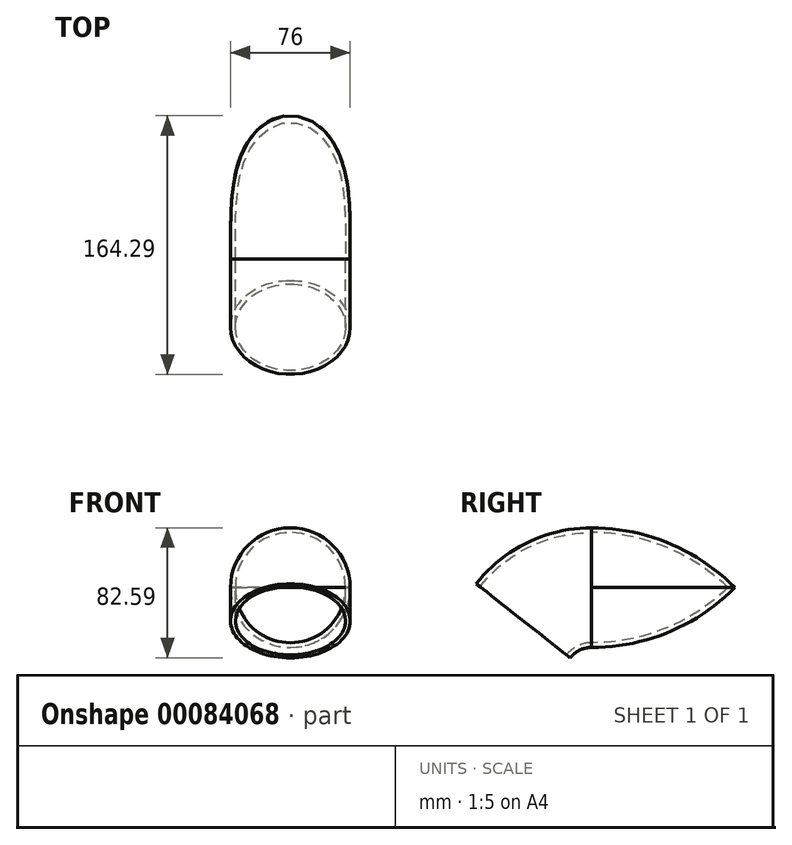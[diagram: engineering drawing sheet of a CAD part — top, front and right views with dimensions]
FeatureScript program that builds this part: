
annotation { "Feature Type Name" : "Feature", "Feature Type Description" : "" }
export const myFeature = defineFeature(function(context is Context, id is Id, definition is map)
    precondition{}
    {
        {
            var Q0;
            Q0=qCreatedBy(makeId("Front.planeOp"),FACE);
            var sketch = newSketch(context, id + "F0", { "sketchPlane" : qUnion([Q0])});
            skCircle(sketch, "E0", {"center": v(0, 0) * mm, "radius": 38 * mm});
            skCircle(sketch, "E1", {"center": v(0, 0) * mm, "radius": 35 * mm});
            skSolve(sketch);
        }
        {
            var Q0;
            Q0=qCreatedBy(makeId("Top.planeOp"),FACE);
            var sketch = newSketch(context, id + "F1", { "sketchPlane" : qUnion([Q0])});
            skLineSegment(sketch, "E2", {"start": v(90, 0) * mm, "end": v(90, 109) * mm, "construction": true});
            skArc(sketch, "E3", {"start": v(0, 0) * mm, "mid": v(26.36, 63.64) * mm, "end": v(90, 90) * mm});
            skSolve(sketch);
        }
        {
            var Q0;
            Q0=makeQuery(id+"F0.imprint","IMPRINT",FACE,{"disambiguationData":[TD([[makeQuery(id+"F0.imprint","IMPRINT",EDGE,{"derivedFrom":sQuery(id+"F0.wireOp",EDGE,"E0")}),1.0]])]});
            var Q1;
            Q1=sQuery(id+"F1.wireOp",EDGE,"E3");
            sweep(context, id + "F2", {"profiles" : qUnion([Q0]), "path" : qUnion([Q1])});
        }
        {
            var Q0;
            Q0=qCreatedBy(makeId("Top.planeOp"),FACE);
            var sketch = newSketch(context, id + "F3", { "sketchPlane" : qUnion([Q0])});
            skLineSegment(sketch, "E4", {"start": v(0, 0) * mm, "end": v(0, 200) * mm});
            skLineSegment(sketch, "E5", {"start": v(0, 200) * mm, "end": v(111.4, 200) * mm});
            skLineSegment(sketch, "E6", {"start": v(111.4, 200) * mm, "end": v(111.4, 0) * mm});
            skLineSegment(sketch, "E7", {"start": v(111.4, 0) * mm, "end": v(0, 0) * mm});
            skSolve(sketch);
        }
        {
            var Q0;
            Q0=makeQuery(id+"F3.imprint","IMPRINT",FACE,{"disambiguationData":[TD([[makeQuery(id+"F3.imprint","IMPRINT",EDGE,{"derivedFrom":sQuery(id+"F3.wireOp",EDGE,"E4")}),-1.0]])]});
            extrude(context, id + "F4", {"entities" : qUnion([Q0]), "operationType" : NewBodyOperationType.REMOVE, "endBound" : BoundingType.SYMMETRIC, "oppositeDirection" : true, "depth" : 200 * mm});
        }
        {
            var Q0;
            Q0=qCreatedBy(makeId("Right.planeOp"),FACE);
            var sketch = newSketch(context, id + "F5", { "sketchPlane" : qUnion([Q0])});
            skLineSegment(sketch, "E8", {"start": v(0, 0) * mm, "end": v(84.07, 0) * mm, "construction": true});
            skSolve(sketch);
        }
        {
            var Q0;
            Q0=makeQuery(id+"F2.opSweep","SWEPT_BODY",BODY,{"disambiguationData":[OSD([sQuery(id+"F0.wireOp",EDGE,"E0"),sQuery(id+"F0.wireOp",EDGE,"E1"),sQuery(id+"F1.wireOp",EDGE,"E3")])]});
            var Q1;
            Q1=sQuery(id+"F5.wireOp",EDGE,"E8");
            transform(context, id + "F6", {"entities" : qUnion([Q0]), "transformType" : TransformType.ROTATION, "transformAxis" : qUnion([Q1]), "angle" : 180 * degree, "makeCopy" : true});
        }
        {
            var Q0;
            Q0=qCreatedBy(makeId("Right.planeOp"),FACE);
            var sketch = newSketch(context, id + "F7", { "sketchPlane" : qUnion([Q0])});
            skArc(sketch, "E9", {"start": v(0, 0) * mm, "mid": v(-24.13, -5.55) * mm, "end": v(-43.42, -21.07) * mm});
            skLineSegment(sketch, "E10", {"start": v(-43.42, -21.07) * mm, "end": v(-80.3, -67.9) * mm});
            skSolve(sketch);
        }
        {
            var Q0;
            Q0=makeQuery(id+"F2.opSweep","SWEPT_BODY",BODY,{"disambiguationData":[OSD([sQuery(id+"F0.wireOp",EDGE,"E0"),sQuery(id+"F0.wireOp",EDGE,"E1"),sQuery(id+"F1.wireOp",EDGE,"E3")])]});
            var Q1;
            Q1=makeQuery(id+"F6.opPattern","COPY",BODY,{"derivedFrom":makeQuery(id+"F2.opSweep","SWEPT_BODY",BODY,{"disambiguationData":[OSD([sQuery(id+"F0.wireOp",EDGE,"E0"),sQuery(id+"F0.wireOp",EDGE,"E1"),sQuery(id+"F1.wireOp",EDGE,"E3")])]}),"instanceName":"1"});
            var Q2;
            Q2=sQuery(id+"F3.wireOp",EDGE,"E4");
            transform(context, id + "F8", {"entities" : qUnion([Q0, Q1]), "transformType" : TransformType.ROTATION, "transformAxis" : qUnion([Q2]), "angle" : 90 * degree, "makeCopy" : false});
        }
        {
            var Q0;
            Q0=makeQuery(id+"F0.imprint","IMPRINT",FACE,{"disambiguationData":[TD([[makeQuery(id+"F0.imprint","IMPRINT",EDGE,{"derivedFrom":sQuery(id+"F0.wireOp",EDGE,"E0")}),1.0]])]});
            var Q1;
            Q1=sQuery(id+"F7.wireOp",EDGE,"E9");
            sweep(context, id + "F9", {"profiles" : qUnion([Q0]), "path" : qUnion([Q1])});
        }
    });
